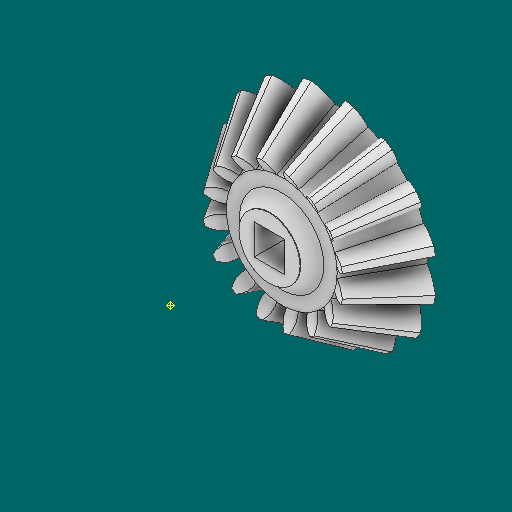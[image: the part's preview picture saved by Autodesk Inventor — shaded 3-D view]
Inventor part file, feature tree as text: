
AUTODESK INVENTOR PART (.ipt)
format: ipt  version: 2023.1 (Build 271208000, 208)  size: 525,824 bytes
history: native  units: in
note: dims shown in document units (in); Inventor stores cm internally (conversion verified against a paired STEP export)
features: other x30, sketch x2
ambient origin geometry x8: Origin, YZ Plane, XZ Plane, XY Plane, X Axis, Y Axis, Z Axis, Center Point
bodies: Solid1 (feature_tree)
feature tree (32):
  other  "Bevel Gear11_MIR.ipt"
  other  "Solid1::Bevel Gear11_MIR.ipt"
  other  "TaggingFeature1"
  other  "Teeth Body Sketch"
  other  "Start Sketch"
  other  "End Sketch"
  other  "End Sketch Right"
  other  "End Sketch Left"
  other  "Body Sketch"
  sketch  "Sketch6"  dims[d0=0.3937in]
  sketch  "Sketch8"  dims[d48=0.0in d49=0.0in d50=90.0deg d52=0.0in d53=0.0in d54=0.0in]
  other  "3D Sketch Right"
  other  "3D Sketch Left"
  other  "Mesh Plane"
  other  "Top Plane"
  other  "Mesh Plane2"
  other  "Tooth Plane"
  other  "End Plane"
  other  "End Plane Right"
  other  "End Plane Left"
  other  "Z Axis_1"
  other  "Top Point"
  other  "Start Point"
  other  "End Point"
  other  "Srf1"
  other  "Srf1::Derived"
  other  "Start plane iMate"
  other  "Mesh iMate2"
  other  "Axis Angle iMate"
  other  "Axis iMate"
  other  "Mesh iMate"
  other  "Intersection iMate"
